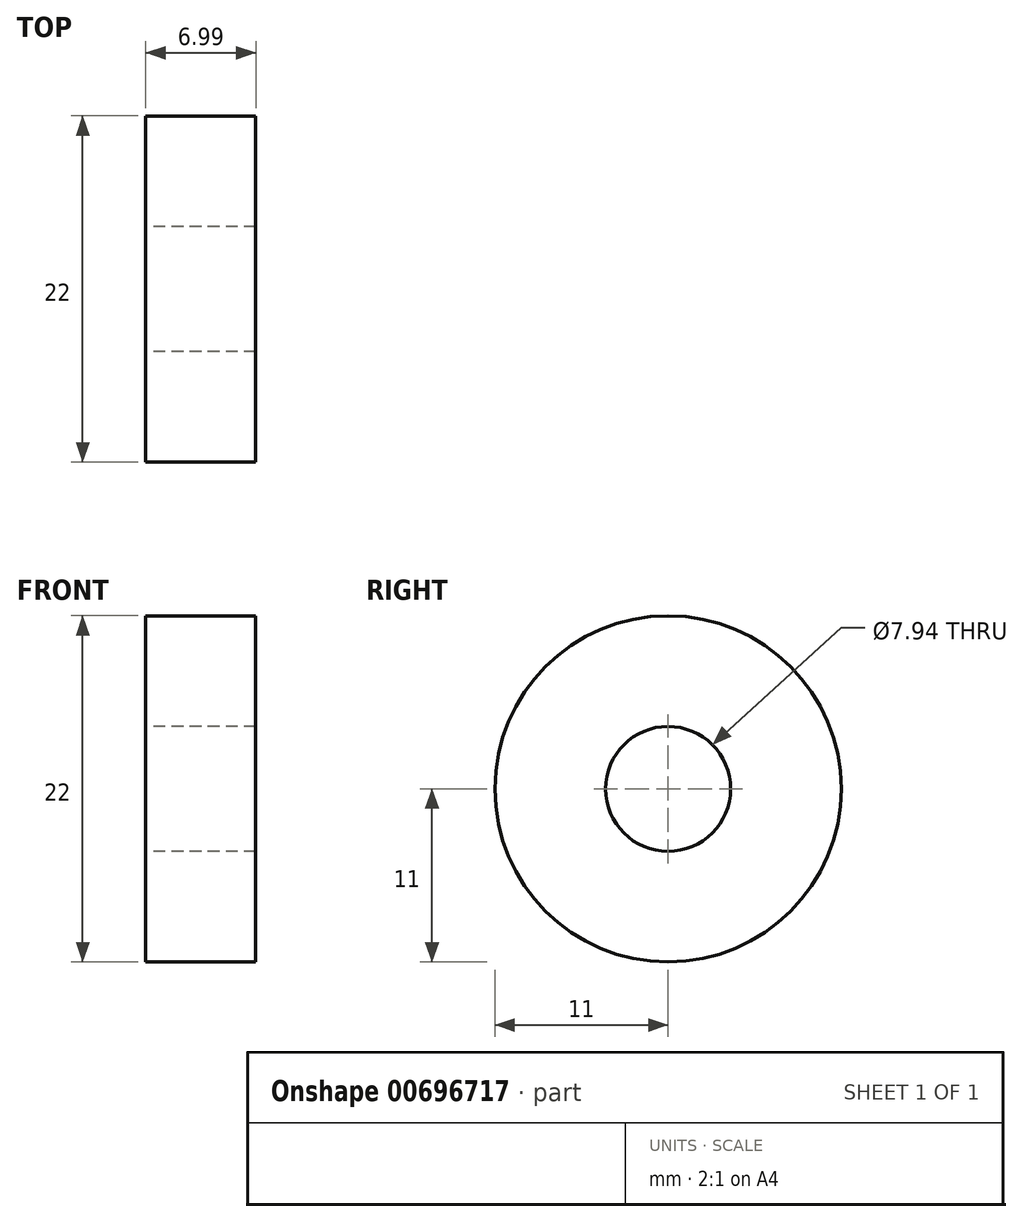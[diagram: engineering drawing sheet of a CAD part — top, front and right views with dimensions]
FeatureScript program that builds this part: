
annotation { "Feature Type Name" : "Feature", "Feature Type Description" : "" }
export const myFeature = defineFeature(function(context is Context, id is Id, definition is map)
    precondition{}
    {
        {
            var Q0;
            Q0=qCreatedBy(makeId("Right.planeOp"),FACE);
            var sketch = newSketch(context, id + "F0", { "sketchPlane" : qUnion([Q0])});
            skCircle(sketch, "E0", {"center": v(0, 0) * mm, "radius": 11 * mm});
            skCircle(sketch, "E1", {"center": v(0, 0) * mm, "radius": 3.97 * mm});
            skSolve(sketch);
        }
        {
            var Q0;
            Q0 = qSketchRegion(id + "F0", true);
            extrude(context, id + "F1", {"entities" : qUnion([Q0]), "depth" : 7 * mm, "offsetDistance" : 25.4 * mm});
        }
    });
